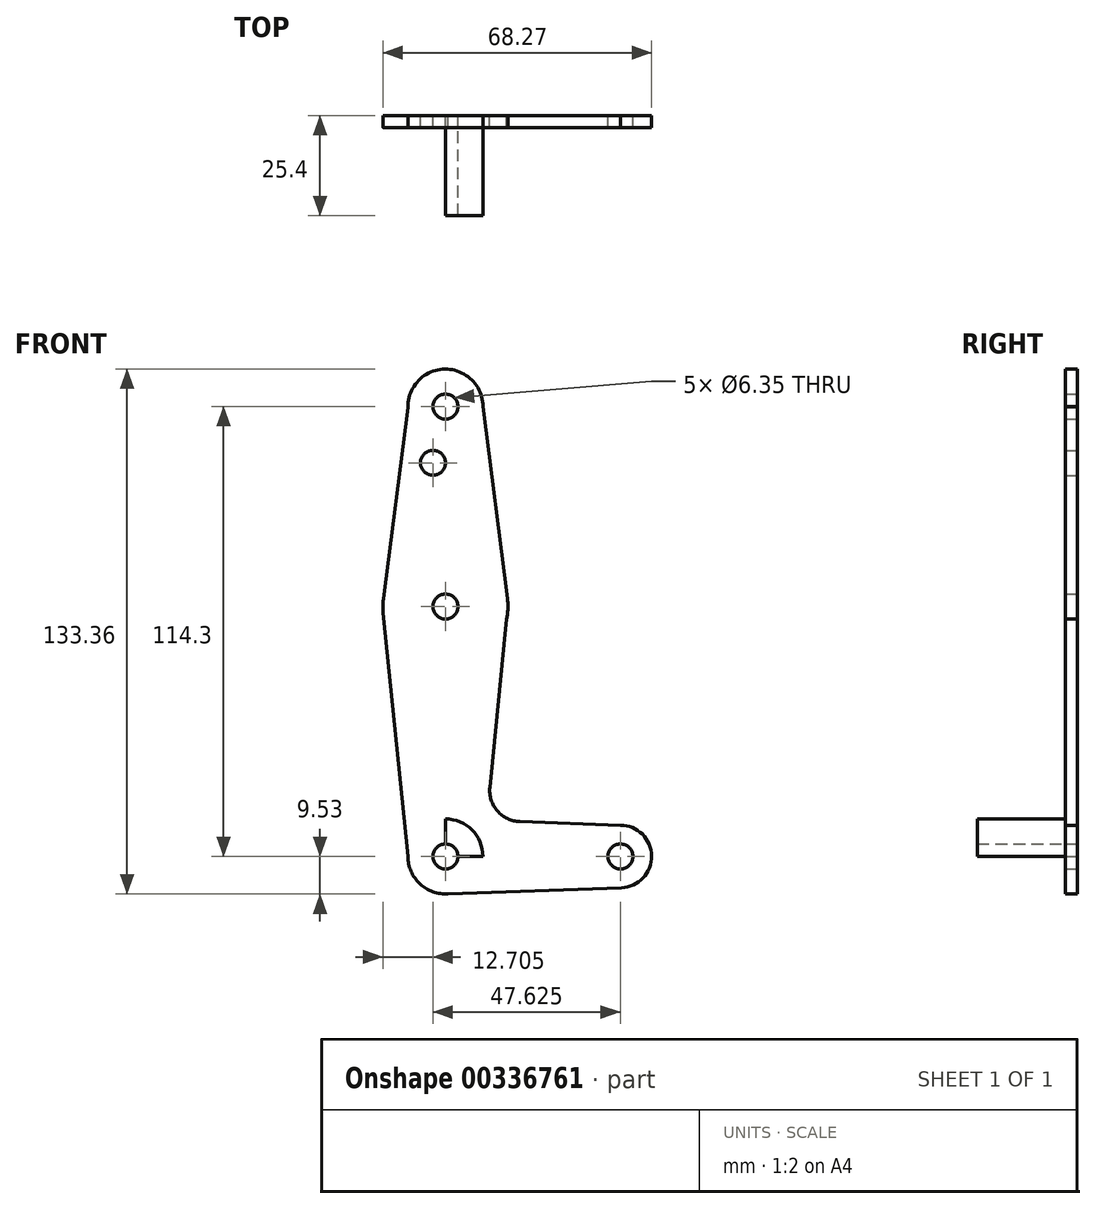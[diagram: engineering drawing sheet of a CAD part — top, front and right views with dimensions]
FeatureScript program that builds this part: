
annotation { "Feature Type Name" : "Feature", "Feature Type Description" : "" }
export const myFeature = defineFeature(function(context is Context, id is Id, definition is map)
    precondition{}
    {
        {
            var Q0;
            Q0=qCreatedBy(makeId("Front.planeOp"),FACE);
            var sketch = newSketch(context, id + "F0", { "sketchPlane" : qUnion([Q0])});
            skLineSegment(sketch, "E0", {"start": v(0, 0) * mm, "end": v(0, 114.3) * mm});
            skCircle(sketch, "E1", {"center": v(0, 114.3) * mm, "radius": 9.53 * mm});
            skCircle(sketch, "E2", {"center": v(0, 0) * mm, "radius": 9.52 * mm});
            skCircle(sketch, "E3", {"center": v(0, 63.5) * mm, "radius": 15.88 * mm});
            skLineSegment(sketch, "E4", {"start": v(0, 0) * mm, "end": v(44.45, 0) * mm});
            skCircle(sketch, "E5", {"center": v(44.45, 0) * mm, "radius": 7.94 * mm});
            skLineSegment(sketch, "E6", {"start": v(-9.52, 114.1) * mm, "end": v(-15.75, 65.52) * mm});
            skLineSegment(sketch, "E7", {"start": v(9.53, 114.3) * mm, "end": v(15.75, 65.5) * mm});
            skLineSegment(sketch, "E8", {"start": v(15.88, 63.5) * mm, "end": v(11.28, 17.59) * mm});
            skLineSegment(sketch, "E9", {"start": v(-9.52, 0) * mm, "end": v(-15.8, 61.9) * mm});
            skLineSegment(sketch, "E10", {"start": v(18.91, 8.85) * mm, "end": v(44.45, 7.94) * mm});
            skLineSegment(sketch, "E11", {"start": v(0, -9.52) * mm, "end": v(44.73, -7.93) * mm});
            skCircle(sketch, "E12", {"center": v(0, 114.3) * mm, "radius": 3.18 * mm});
            skCircle(sketch, "E13", {"center": v(0, 63.5) * mm, "radius": 3.18 * mm});
            skCircle(sketch, "E14", {"center": v(44.45, 0) * mm, "radius": 3.18 * mm});
            skCircle(sketch, "E15", {"center": v(0, 0) * mm, "radius": 3.18 * mm});
            skArc(sketch, "E16.filletArc", {"start": v(11.28, 17.59) * mm, "mid": v(13.2, 11.57) * mm, "end": v(18.91, 8.85) * mm});
            skCircle(sketch, "E17", {"center": v(-3.18, 100.03) * mm, "radius": 3.18 * mm});
            skSolve(sketch);
        }
        {
            var Q0;
            Q0 = qSketchRegion(id + "F0", true);
            extrude(context, id + "F1", {"entities" : qUnion([Q0]), "depth" : 3.05 * mm});
        }
        {
            var Q0;
            {var subQ0=sQuery(id+"F0.wireOp",EDGE,"E15");var subQ1=sQuery(id+"F0.wireOp",EDGE,"E0");var subQ2=makeQuery(id+"F0.imprint","INTERSECT",VERTEX,{"derivedFrom":[subQ1,subQ0]});Q0=makeQuery(id+"F0.imprint","IMPRINT",FACE,{"disambiguationData":[TD([[makeQuery(id+"F0.imprint","IMPRINT",EDGE,{"disambiguationData":[TD([[subQ2,-1.0]])],"derivedFrom":subQ1}),-1.0]])]});}
            extrude(context, id + "F2", {"entities" : qUnion([Q0]), "operationType" : NewBodyOperationType.ADD, "depth" : 25.4 * mm});
        }
    });
